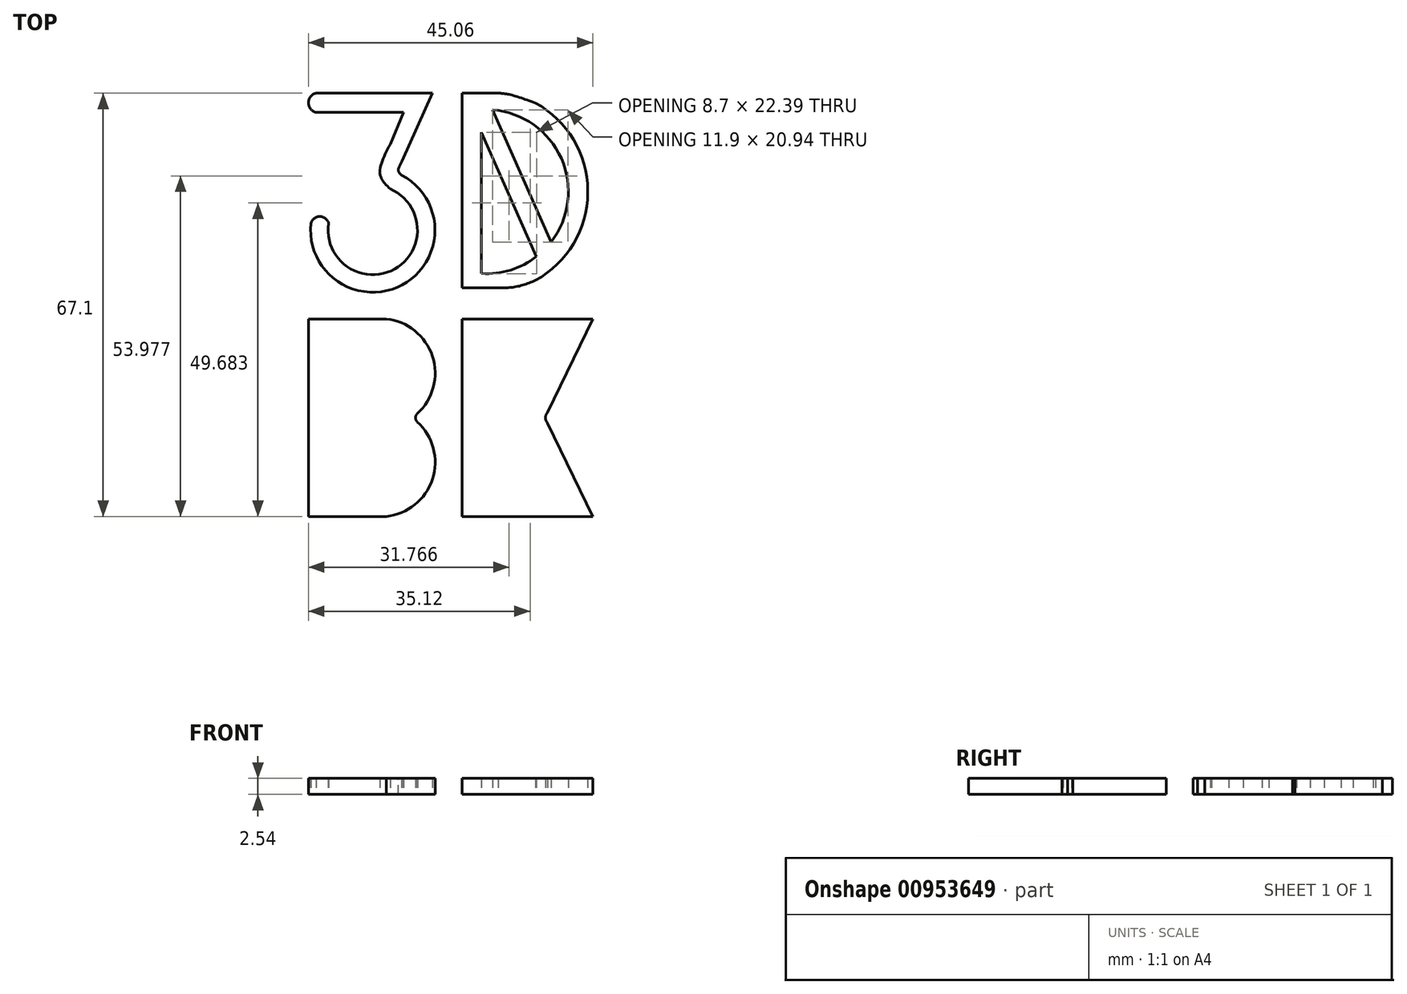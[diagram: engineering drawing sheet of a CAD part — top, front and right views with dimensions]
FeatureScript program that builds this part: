
annotation { "Feature Type Name" : "Feature", "Feature Type Description" : "" }
export const myFeature = defineFeature(function(context is Context, id is Id, definition is map)
    precondition{}
    {
        {
            var Q0;
            Q0=qCreatedBy(makeId("Top.planeOp"),FACE);
            var sketch = newSketch(context, id + "F0", { "sketchPlane" : qUnion([Q0])});
            skLineSegment(sketch, "E0", {"start": v(0, 56.35) * mm, "end": v(0, -56.35) * mm});
            skLineSegment(sketch, "E1", {"start": v(56.35, 0) * mm, "end": v(-56.35, 0) * mm});
            skPoint(sketch, "E2", {"position": v(0, 0) * mm});
            skPoint(sketch, "E3", {"position": v(-22.39, -33.62) * mm});
            skPoint(sketch, "E4", {"position": v(-22.39, 33.48) * mm});
            skPoint(sketch, "E5", {"position": v(21.85, 33.48) * mm});
            skLineSegment(sketch, "E6", {"start": v(1.95, 33.48) * mm, "end": v(7.67, 33.48) * mm});
            skLineSegment(sketch, "E7", {"start": v(21.85, -33.62) * mm, "end": v(1.95, -33.62) * mm});
            skLineSegment(sketch, "E8", {"start": v(21.85, 18.05) * mm, "end": v(21.85, 17.68) * mm});
            skLineSegment(sketch, "E9", {"start": v(-2.74, 33.48) * mm, "end": v(-21.16, 33.48) * mm});
            skLineSegment(sketch, "E10", {"start": v(-22.39, -33.62) * mm, "end": v(-10.07, -33.62) * mm});
            skLineSegment(sketch, "E11", {"start": v(-22.39, -2.3) * mm, "end": v(-22.39, -33.62) * mm});
            skPoint(sketch, "E12", {"position": v(-22.39, 31.95) * mm});
            skPoint(sketch, "E12.positionSnap0", {"position": v(-21.16, 31.95) * mm});
            skArc(sketch, "E13", {"start": v(-21.16, 33.48) * mm, "mid": v(-22.39, 31.95) * mm, "end": v(-21.16, 30.43) * mm});
            skPoint(sketch, "E14", {"position": v(-2.74, 33.48) * mm});
            skPoint(sketch, "E15", {"position": v(-7.3, 30.43) * mm});
            skLineSegment(sketch, "E16", {"start": v(-21.16, 30.43) * mm, "end": v(-7.3, 30.43) * mm});
            skPoint(sketch, "E17", {"position": v(-11.04, 20.68) * mm});
            skPoint(sketch, "E18", {"position": v(-9.45, 18.3) * mm});
            skPoint(sketch, "E19", {"position": v(-9.45, 25.39) * mm});
            skFitSpline(sketch, "E20", {"points": [v(-9.45, 25.39) * mm, v(-11.04, 20.68) * mm, v(-9.45, 18.3) * mm], "startDerivative": vector(-4.65, -9.06) * mm, "endDerivative": vector(5.1, -4.94) * mm});
            skLineSegment(sketch, "E21", {"start": v(-7.3, 30.43) * mm, "end": v(-9.45, 25.39) * mm});
            skPoint(sketch, "E22", {"position": v(-19.2, 12.85) * mm});
            skPoint(sketch, "E23", {"position": v(-12.14, 4.7) * mm});
            skArc(sketch, "E24", {"start": v(-19.2, 12.85) * mm, "mid": v(-8.74, 5.6) * mm, "end": v(-9.45, 18.3) * mm});
            skPoint(sketch, "E25", {"position": v(-8.14, 21.15) * mm});
            skPoint(sketch, "E26", {"position": v(-7.55, 20.43) * mm});
            skPoint(sketch, "E27", {"position": v(-7.55, 22.7) * mm});
            skFitSpline(sketch, "E28", {"points": [v(-7.55, 22.7) * mm, v(-8.14, 21.15) * mm, v(-7.55, 20.43) * mm], "startDerivative": vector(-1.74, -3) * mm, "endDerivative": vector(1.9, -1.47) * mm});
            skLineSegment(sketch, "E29", {"start": v(-2.74, 33.48) * mm, "end": v(-7.55, 22.7) * mm});
            skArc(sketch, "E30.0", {"start": v(-21.98, 12.85) * mm, "mid": v(-7.57, 3.08) * mm, "end": v(-7.62, 20.5) * mm});
            skPoint(sketch, "E31", {"position": v(-21.98, 12.85) * mm});
            skPoint(sketch, "E32", {"position": v(-20.63, 13.93) * mm});
            skArc(sketch, "E33", {"start": v(-19.2, 12.85) * mm, "mid": v(-20.59, 13.94) * mm, "end": v(-21.98, 12.85) * mm});
            skLineSegment(sketch, "E34", {"start": v(1.95, 33.48) * mm, "end": v(1.95, 2.25) * mm});
            skPoint(sketch, "E35", {"position": v(21.85, 18.05) * mm});
            skArc(sketch, "E36", {"start": v(13.56, 3.8) * mm, "mid": v(21.85, 17.87) * mm, "end": v(13.56, 31.93) * mm});
            skPoint(sketch, "E37", {"position": v(7.67, 33.48) * mm});
            skPoint(sketch, "E38", {"position": v(13.56, 31.93) * mm});
            skPoint(sketch, "E39", {"position": v(13.56, 3.8) * mm});
            skArc(sketch, "E40.0", {"start": v(5.03, 4.88) * mm, "mid": v(9.62, 5.44) * mm, "end": v(13.73, 7.58) * mm});
            skLineSegment(sketch, "E40.1", {"start": v(5.03, 27.26) * mm, "end": v(5.03, 4.88) * mm});
            skLineSegment(sketch, "E41", {"start": v(5.03, 27.26) * mm, "end": v(13.73, 7.58) * mm});
            skLineSegment(sketch, "E42", {"start": v(16.04, 9.89) * mm, "end": v(6.78, 30.83) * mm});
            skLineSegment(sketch, "E43", {"start": v(-22.39, -2.3) * mm, "end": v(-10.07, -2.3) * mm});
            skLineSegment(sketch, "E44", {"start": v(1.95, -2.3) * mm, "end": v(1.95, -33.62) * mm});
            skLineSegment(sketch, "E45", {"start": v(1.95, -2.3) * mm, "end": v(22.67, -2.3) * mm});
            skLineSegment(sketch, "E46", {"start": v(22.67, -2.3) * mm, "end": v(15.49, -17.1) * mm});
            skFitSpline(sketch, "E47", {"points": [v(15.49, -17.1) * mm, v(15.2, -17.6) * mm, v(15.17, -17.96) * mm], "startDerivative": vector(-0.63, -0.9) * mm, "endDerivative": vector(0.03, -0.82) * mm});
            skLineSegment(sketch, "E48.MirrorCS", {"start": v(1.95, -33.62) * mm, "end": v(22.67, -33.62) * mm});
            skLineSegment(sketch, "E49.MirrorCS", {"start": v(22.67, -33.62) * mm, "end": v(15.49, -18.82) * mm});
            skFitSpline(sketch, "E50.MirrorCS", {"points": [v(15.49, -18.82) * mm, v(15.2, -18.34) * mm, v(15.17, -17.96) * mm], "startDerivative": vector(-0.63, 0.9) * mm, "endDerivative": vector(0.03, 0.82) * mm});
            skArc(sketch, "E51", {"start": v(-5.17, -17.31) * mm, "mid": v(-2.75, -8.22) * mm, "end": v(-10.07, -2.3) * mm});
            skFitSpline(sketch, "E52", {"points": [v(-5.17, -17.31) * mm, v(-5.38, -17.68) * mm, v(-5.4, -17.96) * mm], "startDerivative": vector(-0.48, -0.68) * mm, "endDerivative": vector(0.02, -0.62) * mm});
            skArc(sketch, "E53.MirrorCS", {"start": v(-5.17, -18.61) * mm, "mid": v(-2.75, -27.7) * mm, "end": v(-10.07, -33.62) * mm});
            skFitSpline(sketch, "E54.MirrorCS", {"points": [v(-5.17, -18.61) * mm, v(-5.38, -18.25) * mm, v(-5.4, -17.96) * mm], "startDerivative": vector(-0.48, 0.68) * mm, "endDerivative": vector(0.02, 0.62) * mm});
            skPoint(sketch, "E55.end.orphan", {"position": v(-10.07, -33.62) * mm});
            skPoint(sketch, "E56.orphan", {"position": v(-10.07, -17.96) * mm});
            skPoint(sketch, "E57.orphan", {"position": v(0, -33.62) * mm});
            skLineSegment(sketch, "E58.MirrorCS", {"start": v(0, 2.62) * mm, "end": v(7.67, 2.62) * mm});
            skArc(sketch, "E59.trimOffspring", {"start": v(16.04, 9.89) * mm, "mid": v(17.67, 23.12) * mm, "end": v(6.78, 30.83) * mm});
            skPoint(sketch, "E60", {"position": v(7.67, 2.62) * mm});
            skFitSpline(sketch, "E61", {"points": [v(13.56, 3.8) * mm, v(10.55, 2.81) * mm, v(7.67, 2.62) * mm], "startDerivative": vector(-5.9, -2.33) * mm, "endDerivative": vector(-5.9, -0.02) * mm});
            skPoint(sketch, "E62.1.internal.snap0", {"position": v(9.38, 17.42) * mm});
            skFitSpline(sketch, "E62", {"points": [v(13.56, 31.93) * mm, v(9.38, 33.27) * mm, v(7.67, 33.48) * mm], "startDerivative": vector(-7.54, 2.7) * mm, "endDerivative": vector(-3.99, 0.22) * mm});
            skPoint(sketch, "E63.orphan", {"position": v(10.87, 2.62) * mm});
            skPoint(sketch, "E64.orphan", {"position": v(0, 33.48) * mm});
            skPoint(sketch, "E65.trimOffspring.start.orphan", {"position": v(21.85, 2.62) * mm});
            skSolve(sketch);
        }
        {
            var Q0;
            Q0=makeQuery(id+"F0.imprint","IMPRINT",FACE,{"disambiguationData":[TD([[makeQuery(id+"F0.imprint","IMPRINT",EDGE,{"derivedFrom":sQuery(id+"F0.wireOp",EDGE,"E9")}),1.0]])]});
            var Q1;
            {var subQ7=sQuery(id+"F0.wireOp",EDGE,"E6");Q1=makeQuery(id+"F0.imprint","IMPRINT",FACE,{"disambiguationData":[TD([[makeQuery(id+"F0.imprint","IMPRINT",EDGE,{"derivedFrom":subQ7}),-1.0]])]});}
            var Q2;
            {var subQ0=sQuery(id+"F0.wireOp",EDGE,"E44");Q2=makeQuery(id+"F0.imprint","IMPRINT",FACE,{"disambiguationData":[TD([[makeQuery(id+"F0.imprint","IMPRINT",EDGE,{"derivedFrom":subQ0}),1.0]])]});}
            var Q3;
            Q3=makeQuery(id+"F0.imprint","IMPRINT",FACE,{"disambiguationData":[TD([[makeQuery(id+"F0.imprint","IMPRINT",EDGE,{"derivedFrom":sQuery(id+"F0.wireOp",EDGE,"E10")}),1.0]])]});
            extrude(context, id + "F1", {"entities" : qUnion([Q0, Q1, Q2, Q3]), "depth" : 2.54 * mm, "offsetDistance" : 25.4 * mm});
        }
    });
